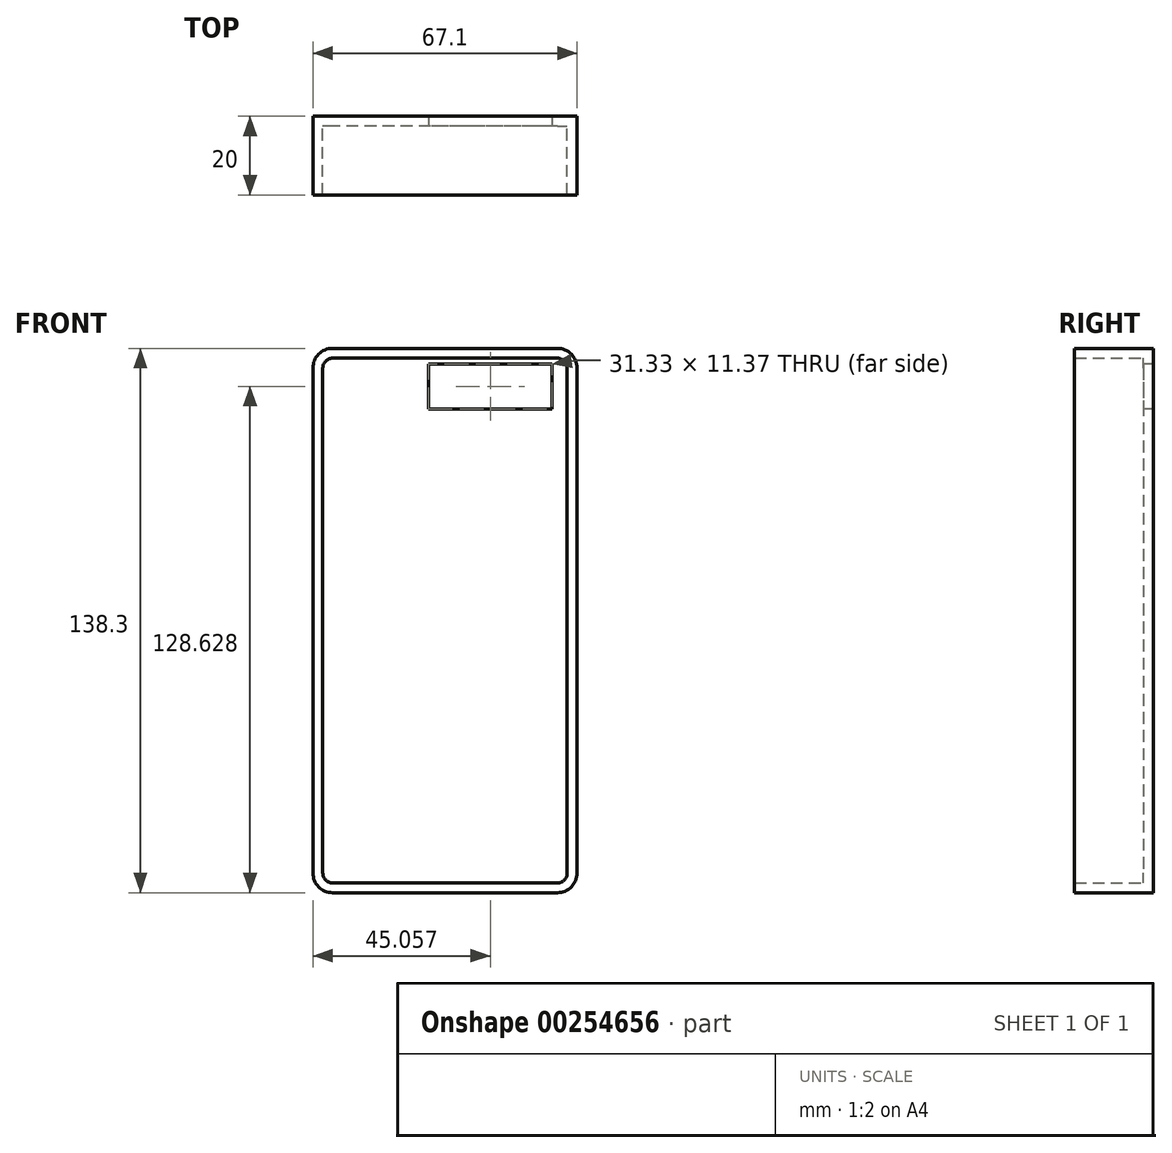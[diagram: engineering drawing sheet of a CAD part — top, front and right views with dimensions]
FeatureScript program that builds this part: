
annotation { "Feature Type Name" : "Feature", "Feature Type Description" : "" }
export const myFeature = defineFeature(function(context is Context, id is Id, definition is map)
    precondition{}
    {
        {
            var Q0;
            Q0=qCreatedBy(makeId("Front.planeOp"),FACE);
            var sketch = newSketch(context, id + "F0", { "sketchPlane" : qUnion([Q0])});
            skLineSegment(sketch, "E0.bottom", {"start": v(33.55, 69.15) * mm, "end": v(-33.55, 69.15) * mm});
            skLineSegment(sketch, "E0.top", {"start": v(33.55, -69.15) * mm, "end": v(-33.55, -69.15) * mm});
            skLineSegment(sketch, "E0.left", {"start": v(33.55, 69.15) * mm, "end": v(33.55, -69.15) * mm});
            skLineSegment(sketch, "E0.right", {"start": v(-33.55, 69.15) * mm, "end": v(-33.55, -69.15) * mm});
            skPoint(sketch, "E0.middle", {"position": v(0, 0) * mm});
            skSolve(sketch);
        }
        {
            var Q0;
            Q0=makeQuery(id+"F0.imprint","IMPRINT",FACE,{"disambiguationData":[TD([[makeQuery(id+"F0.imprint","IMPRINT",EDGE,{"derivedFrom":sQuery(id+"F0.wireOp",EDGE,"E0.bottom")}),1.0]])]});
            extrude(context, id + "F1", {"entities" : qUnion([Q0]), "depth" : 20 * mm, "symmetric" : true});
        }
        {
            var Q0;
            Q0=makeQuery(id+"F1.opExtrude","SWEPT_EDGE",EDGE,{"disambiguationData":[OSD([sQuery(id+"F0.wireOp",EDGE,"E0.bottom"),sQuery(id+"F0.wireOp",EDGE,"E0.right")])]});
            var Q1;
            Q1=makeQuery(id+"F1.opExtrude","SWEPT_EDGE",EDGE,{"disambiguationData":[OSD([sQuery(id+"F0.wireOp",EDGE,"E0.bottom"),sQuery(id+"F0.wireOp",EDGE,"E0.left")])]});
            var Q2;
            Q2=makeQuery(id+"F1.opExtrude","SWEPT_EDGE",EDGE,{"disambiguationData":[OSD([sQuery(id+"F0.wireOp",EDGE,"E0.top"),sQuery(id+"F0.wireOp",EDGE,"E0.left")])]});
            var Q3;
            Q3=makeQuery(id+"F1.opExtrude","SWEPT_EDGE",EDGE,{"disambiguationData":[OSD([sQuery(id+"F0.wireOp",EDGE,"E0.top"),sQuery(id+"F0.wireOp",EDGE,"E0.right")])]});
            fillet(context, id + "F2", {"entities" : qUnion([Q0, Q1, Q2, Q3]), "radius" : 5 * mm, "tangentPropagation" : true, "allowEdgeOverflow" : false});
        }
        {
            var Q0;
            Q0=makeQuery(id+"F1.opExtrude","CAP_FACE",FACE,{"disambiguationData":[OSD([sQuery(id+"F0.wireOp",EDGE,"E0.bottom"),sQuery(id+"F0.wireOp",EDGE,"E0.top"),sQuery(id+"F0.wireOp",EDGE,"E0.left"),sQuery(id+"F0.wireOp",EDGE,"E0.right")])],"isStart":false});
            shell(context, id + "F3", {"entities" : qUnion([Q0]), "thickness" : 2.5 * mm});
        }
        {
            var Q0;
            Q0=qCreatedBy(makeId("Front.planeOp"),FACE);
            var sketch = newSketch(context, id + "F4", { "sketchPlane" : qUnion([Q0])});
            skLineSegment(sketch, "E1.bottom", {"start": v(27.17, 65.16) * mm, "end": v(-4.16, 65.16) * mm});
            skLineSegment(sketch, "E1.top", {"start": v(27.17, 53.8) * mm, "end": v(-4.16, 53.8) * mm});
            skLineSegment(sketch, "E1.left", {"start": v(27.17, 65.16) * mm, "end": v(27.17, 53.8) * mm});
            skLineSegment(sketch, "E1.right", {"start": v(-4.16, 65.16) * mm, "end": v(-4.16, 53.8) * mm});
            skSolve(sketch);
        }
        {
            var Q0;
            Q0=makeQuery(id+"F4.imprint","IMPRINT",FACE,{"disambiguationData":[TD([[makeQuery(id+"F4.imprint","IMPRINT",EDGE,{"derivedFrom":sQuery(id+"F4.wireOp",EDGE,"E1.bottom")}),1.0]])]});
            extrude(context, id + "F5", {"entities" : qUnion([Q0]), "operationType" : NewBodyOperationType.REMOVE, "oppositeDirection" : true, "depth" : 25 * mm});
        }
    });
